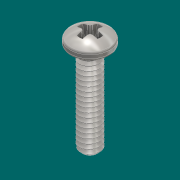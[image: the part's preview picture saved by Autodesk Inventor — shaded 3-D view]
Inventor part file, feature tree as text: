
AUTODESK INVENTOR PART (.ipt)
format: ipt  version: 2016 (Build 200138000, 138)  size: 1,186,816 bytes
history: native  units: mm
features: fillet x1
ambient origin geometry x8: Origin, YZ Plane, XZ Plane, XY Plane, X Axis, Y Axis, Z Axis, Center Point
bodies: Solid1 (feature_tree)
feature tree (1):
  fillet  "Fillet1"  [1 undecoded]
note: 1 required parameter value undecoded (feature->parameter linkage not recoverable at this tier; creation-order binding heuristic only, values carry confidence <= 0.55)
